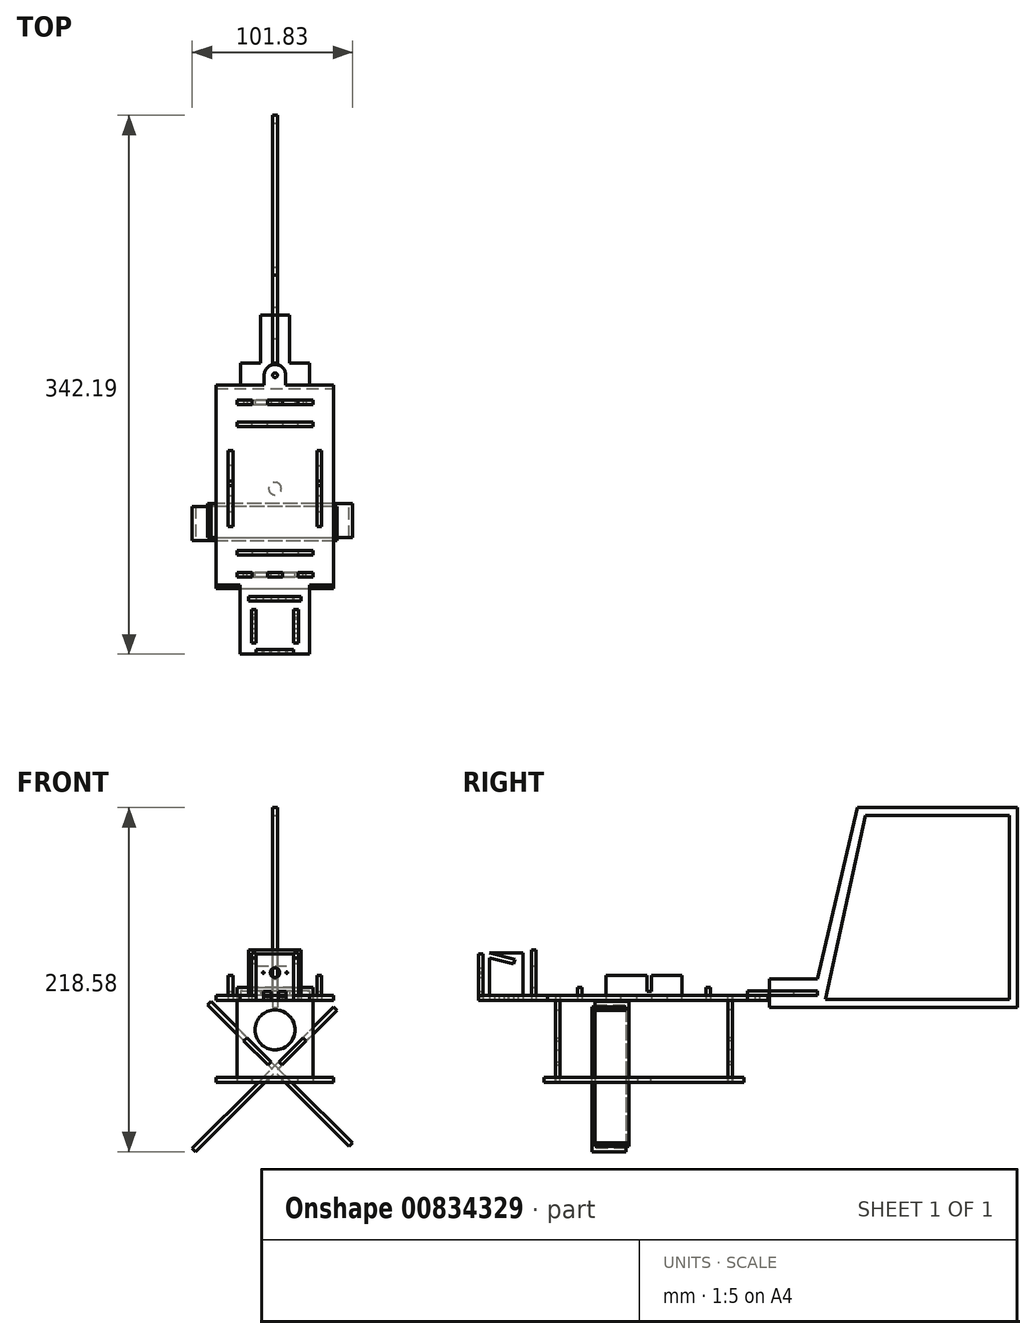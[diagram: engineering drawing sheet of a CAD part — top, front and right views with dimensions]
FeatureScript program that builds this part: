
annotation { "Feature Type Name" : "Feature", "Feature Type Description" : "" }
export const myFeature = defineFeature(function(context is Context, id is Id, definition is map)
    precondition{}
    {
        {
            var Q0;
            Q0=qCreatedBy(makeId("Top.planeOp"),FACE);
            var sketch = newSketch(context, id + "F0", { "sketchPlane" : qUnion([Q0])});
            skLineSegment(sketch, "E0", {"start": v(-22.56, -56.64) * mm, "end": v(-22.56, -53.64) * mm});
            skLineSegment(sketch, "E1", {"start": v(-22.56, -53.64) * mm, "end": v(-12.9, -53.64) * mm});
            skLineSegment(sketch, "E2", {"start": v(-12.9, -53.64) * mm, "end": v(-12.9, -56.64) * mm});
            skLineSegment(sketch, "E3", {"start": v(-3.25, -56.64) * mm, "end": v(-3.25, -53.64) * mm});
            skLineSegment(sketch, "E4", {"start": v(-3.25, -53.64) * mm, "end": v(6.4, -53.64) * mm});
            skLineSegment(sketch, "E5", {"start": v(6.4, -53.64) * mm, "end": v(6.4, -56.64) * mm});
            skLineSegment(sketch, "E6", {"start": v(16.05, -56.64) * mm, "end": v(16.05, -53.64) * mm});
            skLineSegment(sketch, "E7", {"start": v(16.05, -53.64) * mm, "end": v(25.7, -53.64) * mm});
            skLineSegment(sketch, "E8", {"start": v(25.7, -53.64) * mm, "end": v(25.7, -56.64) * mm});
            skLineSegment(sketch, "E9", {"start": v(-22.56, -56.64) * mm, "end": v(-12.9, -56.64) * mm});
            skLineSegment(sketch, "E10", {"start": v(-3.25, -56.64) * mm, "end": v(6.4, -56.64) * mm});
            skLineSegment(sketch, "E11", {"start": v(16.05, -56.64) * mm, "end": v(25.7, -56.64) * mm});
            skLineSegment(sketch, "E12", {"start": v(-22.56, 53.04) * mm, "end": v(-22.56, 56.04) * mm});
            skLineSegment(sketch, "E13", {"start": v(-22.56, 56.04) * mm, "end": v(-12.9, 56.04) * mm});
            skLineSegment(sketch, "E14", {"start": v(-12.9, 56.04) * mm, "end": v(-12.9, 53.04) * mm});
            skLineSegment(sketch, "E15", {"start": v(-3.25, 53.04) * mm, "end": v(-3.25, 56.04) * mm});
            skLineSegment(sketch, "E16", {"start": v(-3.25, 56.04) * mm, "end": v(6.4, 56.04) * mm});
            skLineSegment(sketch, "E17", {"start": v(6.4, 56.04) * mm, "end": v(6.4, 53.04) * mm});
            skLineSegment(sketch, "E18", {"start": v(16.05, 53.04) * mm, "end": v(16.05, 56.04) * mm});
            skLineSegment(sketch, "E19", {"start": v(16.05, 56.04) * mm, "end": v(25.7, 56.04) * mm});
            skLineSegment(sketch, "E20", {"start": v(25.7, 56.04) * mm, "end": v(25.7, 53.04) * mm});
            skLineSegment(sketch, "E21", {"start": v(-22.56, 53.04) * mm, "end": v(-12.9, 53.04) * mm});
            skLineSegment(sketch, "E22", {"start": v(-3.25, 53.04) * mm, "end": v(6.4, 53.04) * mm});
            skLineSegment(sketch, "E23", {"start": v(16.05, 53.04) * mm, "end": v(25.7, 53.04) * mm});
            skLineSegment(sketch, "E24", {"start": v(38.88, 63.2) * mm, "end": v(38.88, -63.8) * mm});
            skLineSegment(sketch, "E25", {"start": v(-35.74, 63.2) * mm, "end": v(-35.74, -63.8) * mm});
            skLineSegment(sketch, "E26", {"start": v(-35.74, -63.8) * mm, "end": v(38.88, -63.8) * mm});
            skLineSegment(sketch, "E27", {"start": v(-35.74, 63.2) * mm, "end": v(38.88, 63.2) * mm});
            skCircle(sketch, "E28", {"center": v(1.57, -0.3) * mm, "radius": 4 * mm});
            skSolve(sketch);
        }
        {
            var Q0;
            Q0=makeQuery(id+"F0.imprint","IMPRINT",FACE,{"disambiguationData":[TD([[makeQuery(id+"F0.imprint","IMPRINT",EDGE,{"derivedFrom":sQuery(id+"F0.wireOp",EDGE,"E0")}),1.0]])]});
            extrude(context, id + "F1", {"entities" : qUnion([Q0]), "depth" : 3 * mm, "offsetDistance" : 25.4 * mm});
        }
        {
            var Q0;
            Q0=makeQuery(id+"F1.opExtrude","SWEPT_FACE",FACE,{"disambiguationData":[OSD([sQuery(id+"F0.wireOp",EDGE,"E1")])]});
            var sketch = newSketch(context, id + "F2", { "sketchPlane" : qUnion([Q0])});
            skPoint(sketch, "E29.0", {"position": v(-22.56, 3) * mm});
            skPoint(sketch, "E30.0", {"position": v(-12.9, 3) * mm});
            skPoint(sketch, "E31.0", {"position": v(-12.9, 0) * mm});
            skPoint(sketch, "E32.0", {"position": v(-22.56, 0) * mm});
            skPoint(sketch, "E33.0", {"position": v(6.4, 3) * mm});
            skPoint(sketch, "E34.0", {"position": v(-3.25, 3) * mm});
            skPoint(sketch, "E35.0", {"position": v(-3.25, 0) * mm});
            skPoint(sketch, "E36.0", {"position": v(6.4, 0) * mm});
            skPoint(sketch, "E37.0", {"position": v(25.7, 3) * mm});
            skPoint(sketch, "E38.0", {"position": v(16.05, 3) * mm});
            skPoint(sketch, "E39.0", {"position": v(16.05, 0) * mm});
            skPoint(sketch, "E40.0", {"position": v(25.7, 0) * mm});
            skLineSegment(sketch, "E41", {"start": v(-3, 10.92) * mm, "end": v(-0.97, 12.95) * mm});
            skLineSegment(sketch, "E42", {"start": v(6.14, 10.92) * mm, "end": v(4.11, 12.95) * mm});
            skLineSegment(sketch, "E43", {"start": v(-0.97, 12.95) * mm, "end": v(-16.24, 28.22) * mm});
            skLineSegment(sketch, "E44", {"start": v(-3, 10.92) * mm, "end": v(-18.27, 26.19) * mm});
            skLineSegment(sketch, "E45", {"start": v(-18.27, 26.19) * mm, "end": v(-16.24, 28.22) * mm});
            skLineSegment(sketch, "E46", {"start": v(4.11, 12.95) * mm, "end": v(19.38, 28.22) * mm});
            skLineSegment(sketch, "E47", {"start": v(6.14, 10.92) * mm, "end": v(21.4, 26.19) * mm});
            skLineSegment(sketch, "E48", {"start": v(21.4, 26.19) * mm, "end": v(19.38, 28.22) * mm});
            skCircle(sketch, "E49", {"center": v(1.57, 33.27) * mm, "radius": 12.7 * mm});
            skLineSegment(sketch, "E50", {"start": v(25.7, 0) * mm, "end": v(16.05, 0) * mm});
            skLineSegment(sketch, "E51", {"start": v(16.05, 0) * mm, "end": v(16.05, 3) * mm});
            skLineSegment(sketch, "E52", {"start": v(16.05, 3) * mm, "end": v(6.4, 3) * mm});
            skLineSegment(sketch, "E53", {"start": v(6.4, 3) * mm, "end": v(6.4, 0) * mm});
            skLineSegment(sketch, "E54", {"start": v(6.4, 0) * mm, "end": v(-3.25, 0) * mm});
            skLineSegment(sketch, "E55", {"start": v(-3.25, 0) * mm, "end": v(-3.25, 3) * mm});
            skLineSegment(sketch, "E56", {"start": v(-3.25, 3) * mm, "end": v(-12.9, 3) * mm});
            skLineSegment(sketch, "E57", {"start": v(-12.9, 3) * mm, "end": v(-12.9, 0) * mm});
            skLineSegment(sketch, "E58", {"start": v(-12.9, 0) * mm, "end": v(-22.56, 0) * mm});
            skLineSegment(sketch, "E59", {"start": v(-22.56, 55.07) * mm, "end": v(-12.9, 55.07) * mm});
            skLineSegment(sketch, "E60", {"start": v(-12.9, 55.07) * mm, "end": v(-12.9, 52.07) * mm});
            skLineSegment(sketch, "E61", {"start": v(-12.9, 52.07) * mm, "end": v(-3.25, 52.07) * mm});
            skLineSegment(sketch, "E62", {"start": v(-3.25, 52.07) * mm, "end": v(-3.25, 55.07) * mm});
            skLineSegment(sketch, "E63", {"start": v(-3.25, 55.07) * mm, "end": v(6.4, 55.07) * mm});
            skLineSegment(sketch, "E64", {"start": v(6.4, 55.07) * mm, "end": v(6.4, 52.07) * mm});
            skLineSegment(sketch, "E65", {"start": v(6.4, 52.07) * mm, "end": v(16.05, 52.07) * mm});
            skLineSegment(sketch, "E66", {"start": v(16.05, 52.07) * mm, "end": v(16.05, 55.07) * mm});
            skLineSegment(sketch, "E67", {"start": v(16.05, 55.07) * mm, "end": v(25.7, 55.07) * mm});
            skLineSegment(sketch, "E68", {"start": v(-22.56, 55.07) * mm, "end": v(-22.56, 0) * mm});
            skLineSegment(sketch, "E69", {"start": v(25.7, 55.07) * mm, "end": v(25.7, 0) * mm});
            skSolve(sketch);
        }
        {
            var Q0;
            Q0=makeQuery(id+"F2.imprint","IMPRINT",FACE,{"disambiguationData":[TD([[makeQuery(id+"F2.imprint","IMPRINT",EDGE,{"derivedFrom":sQuery(id+"F2.wireOp",EDGE,"E41")}),-1.0]])]});
            extrude(context, id + "F3", {"entities" : qUnion([Q0]), "depth" : 3 * mm, "offsetDistance" : 25.4 * mm});
        }
        {
            var Q0;
            Q0=makeQuery(id+"F1.opExtrude","SWEPT_FACE",FACE,{"disambiguationData":[OSD([sQuery(id+"F0.wireOp",EDGE,"E23")])]});
            var sketch = newSketch(context, id + "F4", { "sketchPlane" : qUnion([Q0])});
            skLineSegment(sketch, "E70", {"start": v(-6.14, 10.92) * mm, "end": v(-4.11, 12.95) * mm});
            skLineSegment(sketch, "E71", {"start": v(3, 10.92) * mm, "end": v(0.97, 12.95) * mm});
            skLineSegment(sketch, "E72", {"start": v(-4.11, 12.95) * mm, "end": v(-19.38, 28.22) * mm});
            skLineSegment(sketch, "E73", {"start": v(-6.14, 10.92) * mm, "end": v(-21.4, 26.19) * mm});
            skLineSegment(sketch, "E74", {"start": v(-21.4, 26.19) * mm, "end": v(-19.38, 28.22) * mm});
            skLineSegment(sketch, "E75", {"start": v(0.97, 12.95) * mm, "end": v(16.24, 28.22) * mm});
            skLineSegment(sketch, "E76", {"start": v(3, 10.92) * mm, "end": v(18.27, 26.19) * mm});
            skLineSegment(sketch, "E77", {"start": v(18.27, 26.19) * mm, "end": v(16.24, 28.22) * mm});
            skCircle(sketch, "E78", {"center": v(-1.57, 33.27) * mm, "radius": 12.7 * mm});
            skLineSegment(sketch, "E79", {"start": v(22.56, 0) * mm, "end": v(12.9, 0) * mm});
            skLineSegment(sketch, "E80", {"start": v(12.9, 0) * mm, "end": v(12.9, 3) * mm});
            skLineSegment(sketch, "E81", {"start": v(12.9, 3) * mm, "end": v(3.26, 3) * mm});
            skLineSegment(sketch, "E82", {"start": v(3.26, 3) * mm, "end": v(3.26, 0) * mm});
            skLineSegment(sketch, "E83", {"start": v(3.26, 0) * mm, "end": v(-6.4, 0) * mm});
            skLineSegment(sketch, "E84", {"start": v(-6.4, 0) * mm, "end": v(-6.4, 3) * mm});
            skLineSegment(sketch, "E85", {"start": v(-6.4, 3) * mm, "end": v(-16.05, 3) * mm});
            skLineSegment(sketch, "E86", {"start": v(-16.05, 3) * mm, "end": v(-16.05, 0) * mm});
            skLineSegment(sketch, "E87", {"start": v(-16.05, 0) * mm, "end": v(-25.7, 0) * mm});
            skLineSegment(sketch, "E88", {"start": v(-25.7, 55.07) * mm, "end": v(-16.05, 55.07) * mm});
            skLineSegment(sketch, "E89", {"start": v(-16.05, 55.07) * mm, "end": v(-16.05, 52.07) * mm});
            skLineSegment(sketch, "E90", {"start": v(-16.05, 52.07) * mm, "end": v(-6.4, 52.07) * mm});
            skLineSegment(sketch, "E91", {"start": v(-6.4, 52.07) * mm, "end": v(-6.4, 55.07) * mm});
            skLineSegment(sketch, "E92", {"start": v(-6.4, 55.07) * mm, "end": v(3.26, 55.07) * mm});
            skLineSegment(sketch, "E93", {"start": v(3.26, 55.07) * mm, "end": v(3.26, 52.07) * mm});
            skLineSegment(sketch, "E94", {"start": v(3.26, 52.07) * mm, "end": v(12.9, 52.07) * mm});
            skLineSegment(sketch, "E95", {"start": v(12.9, 52.07) * mm, "end": v(12.9, 55.07) * mm});
            skLineSegment(sketch, "E96", {"start": v(12.9, 55.07) * mm, "end": v(22.56, 55.07) * mm});
            skLineSegment(sketch, "E97", {"start": v(-25.7, 55.07) * mm, "end": v(-25.7, 0) * mm});
            skLineSegment(sketch, "E98", {"start": v(22.56, 55.07) * mm, "end": v(22.56, 0) * mm});
            skPoint(sketch, "E99.0", {"position": v(-25.7, 3) * mm});
            skPoint(sketch, "E100.0", {"position": v(-16.05, 3) * mm});
            skPoint(sketch, "E101.0", {"position": v(-16.05, 0) * mm});
            skPoint(sketch, "E102.0", {"position": v(-25.7, 0) * mm});
            skPoint(sketch, "E103.0", {"position": v(-6.4, 3) * mm});
            skPoint(sketch, "E104.0", {"position": v(-6.4, 0) * mm});
            skPoint(sketch, "E105.0", {"position": v(3.25, 3) * mm});
            skPoint(sketch, "E106.0", {"position": v(3.25, 0) * mm});
            skPoint(sketch, "E107.0", {"position": v(22.56, 0) * mm});
            skPoint(sketch, "E108.0", {"position": v(22.56, 3) * mm});
            skPoint(sketch, "E109.0", {"position": v(12.9, 3) * mm});
            skPoint(sketch, "E110.0", {"position": v(12.9, 0) * mm});
            skSolve(sketch);
        }
        {
            var Q0;
            Q0=makeQuery(id+"F4.imprint","IMPRINT",FACE,{"disambiguationData":[TD([[makeQuery(id+"F4.imprint","IMPRINT",EDGE,{"derivedFrom":sQuery(id+"F4.wireOp",EDGE,"E70")}),-1.0]])]});
            extrude(context, id + "F5", {"entities" : qUnion([Q0]), "depth" : 3 * mm, "offsetDistance" : 25.4 * mm});
        }
        {
            var Q0;
            Q0=makeQuery(id+"F5.opExtrude","SWEPT_FACE",FACE,{"disambiguationData":[OSD([sQuery(id+"F4.wireOp",EDGE,"E76")])]});
            var sketch = newSketch(context, id + "F6", { "sketchPlane" : qUnion([Q0])});
            skLineSegment(sketch, "E111", {"start": v(-31.44, 63.75) * mm, "end": v(-9.85, 63.75) * mm});
            skLineSegment(sketch, "E112", {"start": v(-31.44, 63.75) * mm, "end": v(-31.44, -63.25) * mm});
            skLineSegment(sketch, "E113", {"start": v(-31.44, -63.25) * mm, "end": v(-9.85, -63.25) * mm});
            skLineSegment(sketch, "E114", {"start": v(-9.85, -63.25) * mm, "end": v(-9.85, 63.75) * mm});
            skPoint(sketch, "E115.0", {"position": v(9.46, 59.18) * mm});
            skPoint(sketch, "E116.0", {"position": v(9.46, 62.18) * mm});
            skPoint(sketch, "E117.0", {"position": v(-9.85, -53.64) * mm});
            skPoint(sketch, "E118.0", {"position": v(-9.85, -56.64) * mm});
            skPoint(sketch, "E119.0", {"position": v(-31.43, 56.04) * mm});
            skPoint(sketch, "E120.0", {"position": v(-31.43, 53.04) * mm});
            skPoint(sketch, "E121.0", {"position": v(-9.84, 53.04) * mm});
            skPoint(sketch, "E122.0", {"position": v(-9.84, 56.04) * mm});
            skSolve(sketch);
        }
        {
            var Q0;
            {var subQ5=sQuery(id+"F6.wireOp",EDGE,"E111");Q0=makeQuery(id+"F6.imprint","IMPRINT",FACE,{"disambiguationData":[TD([[makeQuery(id+"F6.imprint","IMPRINT",EDGE,{"derivedFrom":subQ5}),-1.0]])]});}
            extrude(context, id + "F7", {"entities" : qUnion([Q0]), "depth" : 3 * mm, "offsetDistance" : 25.4 * mm});
        }
        {
            var Q0;
            Q0=makeQuery(id+"F5.opExtrude","SWEPT_FACE",FACE,{"disambiguationData":[OSD([sQuery(id+"F4.wireOp",EDGE,"E73")])]});
            var sketch = newSketch(context, id + "F8", { "sketchPlane" : qUnion([Q0])});
            skLineSegment(sketch, "E123", {"start": v(11.73, 61.21) * mm, "end": v(33.32, 61.21) * mm});
            skLineSegment(sketch, "E124", {"start": v(11.73, 61.21) * mm, "end": v(11.73, -65.79) * mm});
            skLineSegment(sketch, "E125", {"start": v(11.73, -65.79) * mm, "end": v(33.32, -65.79) * mm});
            skLineSegment(sketch, "E126", {"start": v(33.32, -65.79) * mm, "end": v(33.32, 61.21) * mm});
            skPoint(sketch, "E127.0", {"position": v(33.66, 53.04) * mm});
            skPoint(sketch, "E128.0", {"position": v(33.66, 56.04) * mm});
            skPoint(sketch, "E129.0", {"position": v(12.07, 53.04) * mm});
            skPoint(sketch, "E130.0", {"position": v(12.07, 56.04) * mm});
            skPoint(sketch, "E131.0", {"position": v(12.07, -53.64) * mm});
            skPoint(sketch, "E132.0", {"position": v(12.07, -56.64) * mm});
            skPoint(sketch, "E133.0", {"position": v(33.66, -56.64) * mm});
            skPoint(sketch, "E134.0", {"position": v(33.66, -53.64) * mm});
            skSolve(sketch);
        }
        {
            var Q0;
            {var subQ5=sQuery(id+"F8.wireOp",EDGE,"E123");Q0=makeQuery(id+"F8.imprint","IMPRINT",FACE,{"disambiguationData":[TD([[makeQuery(id+"F8.imprint","IMPRINT",EDGE,{"derivedFrom":subQ5}),-1.0]])]});}
            extrude(context, id + "F9", {"entities" : qUnion([Q0]), "depth" : 3 * mm, "offsetDistance" : 25.4 * mm});
        }
        {
            var Q0;
            Q0=makeQuery(id+"F5.opExtrude","SWEPT_FACE",FACE,{"disambiguationData":[OSD([sQuery(id+"F4.wireOp",EDGE,"E90")])]});
            var sketch = newSketch(context, id + "F10", { "sketchPlane" : qUnion([Q0])});
            skLineSegment(sketch, "E135", {"start": v(8.72, -105.41) * mm, "end": v(3.95, -105.41) * mm});
            skLineSegment(sketch, "E136", {"start": v(3.95, -105.41) * mm, "end": v(3.95, -102.41) * mm});
            skLineSegment(sketch, "E137", {"start": v(3.95, -102.41) * mm, "end": v(-0.81, -102.41) * mm});
            skLineSegment(sketch, "E138", {"start": v(-0.81, -102.41) * mm, "end": v(-0.81, -105.41) * mm});
            skLineSegment(sketch, "E139", {"start": v(-0.81, -105.41) * mm, "end": v(-5.58, -105.41) * mm});
            skLineSegment(sketch, "E140", {"start": v(-5.58, -105.41) * mm, "end": v(-5.58, -102.41) * mm});
            skLineSegment(sketch, "E141", {"start": v(-5.58, -102.41) * mm, "end": v(-10.34, -102.41) * mm});
            skLineSegment(sketch, "E142", {"start": v(-10.34, -102.41) * mm, "end": v(-10.34, -105.41) * mm});
            skLineSegment(sketch, "E143", {"start": v(8.72, -105.41) * mm, "end": v(8.72, -102.41) * mm});
            skLineSegment(sketch, "E144", {"start": v(8.72, -102.41) * mm, "end": v(13.48, -102.41) * mm});
            skLineSegment(sketch, "E145", {"start": v(13.48, -102.41) * mm, "end": v(13.48, -105.41) * mm});
            skLineSegment(sketch, "E146", {"start": v(-10.34, -105.41) * mm, "end": v(-20.5, -105.41) * mm});
            skLineSegment(sketch, "E147", {"start": v(-20.5, -105.41) * mm, "end": v(-20.5, -61.67) * mm});
            skLineSegment(sketch, "E148", {"start": v(13.48, -105.41) * mm, "end": v(23.64, -105.41) * mm});
            skLineSegment(sketch, "E149", {"start": v(23.64, -105.41) * mm, "end": v(23.64, -61.67) * mm});
            skLineSegment(sketch, "E150", {"start": v(8.72, -71.83) * mm, "end": v(3.95, -71.83) * mm});
            skLineSegment(sketch, "E151", {"start": v(3.95, -71.83) * mm, "end": v(3.95, -68.83) * mm});
            skLineSegment(sketch, "E152", {"start": v(-0.81, -68.83) * mm, "end": v(-0.81, -71.83) * mm});
            skLineSegment(sketch, "E153", {"start": v(-0.81, -71.83) * mm, "end": v(-5.58, -71.83) * mm});
            skLineSegment(sketch, "E154", {"start": v(-5.58, -71.83) * mm, "end": v(-5.58, -68.83) * mm});
            skLineSegment(sketch, "E155", {"start": v(-10.34, -68.83) * mm, "end": v(-10.34, -71.83) * mm});
            skLineSegment(sketch, "E156", {"start": v(8.72, -71.83) * mm, "end": v(8.72, -68.83) * mm});
            skLineSegment(sketch, "E157", {"start": v(13.48, -68.83) * mm, "end": v(13.48, -71.83) * mm});
            skLineSegment(sketch, "E158", {"start": v(-10.34, -71.83) * mm, "end": v(-15.1, -71.83) * mm});
            skLineSegment(sketch, "E159", {"start": v(-15.1, -71.83) * mm, "end": v(-15.1, -68.83) * mm});
            skLineSegment(sketch, "E160", {"start": v(13.48, -71.83) * mm, "end": v(18.25, -71.83) * mm});
            skLineSegment(sketch, "E161", {"start": v(18.25, -71.83) * mm, "end": v(18.25, -68.83) * mm});
            skLineSegment(sketch, "E162", {"start": v(-15.1, -68.83) * mm, "end": v(-10.34, -68.83) * mm});
            skLineSegment(sketch, "E163", {"start": v(-5.58, -68.83) * mm, "end": v(-0.81, -68.83) * mm});
            skLineSegment(sketch, "E164", {"start": v(3.95, -68.83) * mm, "end": v(8.72, -68.83) * mm});
            skLineSegment(sketch, "E165", {"start": v(13.48, -68.83) * mm, "end": v(18.25, -68.83) * mm});
            skLineSegment(sketch, "E166", {"start": v(-10.34, -92.25) * mm, "end": v(-13.34, -92.25) * mm});
            skLineSegment(sketch, "E167", {"start": v(-13.34, -92.25) * mm, "end": v(-13.34, -89.23) * mm});
            skLineSegment(sketch, "E168", {"start": v(-13.34, -89.23) * mm, "end": v(-10.34, -89.23) * mm});
            skLineSegment(sketch, "E169", {"start": v(-10.34, -86.23) * mm, "end": v(-13.34, -86.23) * mm});
            skLineSegment(sketch, "E170", {"start": v(-13.34, -86.23) * mm, "end": v(-13.34, -83.23) * mm});
            skLineSegment(sketch, "E171", {"start": v(-13.34, -83.23) * mm, "end": v(-10.34, -83.23) * mm});
            skLineSegment(sketch, "E172", {"start": v(-10.34, -83.23) * mm, "end": v(-10.34, -86.23) * mm});
            skLineSegment(sketch, "E173", {"start": v(-10.34, -92.25) * mm, "end": v(-10.34, -89.23) * mm});
            skLineSegment(sketch, "E174", {"start": v(-20.5, -61.67) * mm, "end": v(-35.74, -61.67) * mm});
            skLineSegment(sketch, "E175", {"start": v(38.88, -61.67) * mm, "end": v(23.64, -61.67) * mm});
            skLineSegment(sketch, "E176", {"start": v(-22.56, -56.64) * mm, "end": v(-22.56, -53.64) * mm});
            skLineSegment(sketch, "E177", {"start": v(-22.56, -53.64) * mm, "end": v(-12.9, -53.64) * mm});
            skLineSegment(sketch, "E178", {"start": v(-12.9, -53.64) * mm, "end": v(-12.9, -56.64) * mm});
            skLineSegment(sketch, "E179", {"start": v(-3.25, -56.64) * mm, "end": v(-3.25, -53.64) * mm});
            skLineSegment(sketch, "E180", {"start": v(-3.25, -53.64) * mm, "end": v(6.4, -53.64) * mm});
            skLineSegment(sketch, "E181", {"start": v(6.4, -53.64) * mm, "end": v(6.4, -56.64) * mm});
            skLineSegment(sketch, "E182", {"start": v(16.05, -56.64) * mm, "end": v(16.05, -53.64) * mm});
            skLineSegment(sketch, "E183", {"start": v(16.05, -53.64) * mm, "end": v(25.7, -53.64) * mm});
            skLineSegment(sketch, "E184", {"start": v(25.7, -53.64) * mm, "end": v(25.7, -56.64) * mm});
            skLineSegment(sketch, "E185", {"start": v(-22.56, -56.64) * mm, "end": v(-12.9, -56.64) * mm});
            skLineSegment(sketch, "E186", {"start": v(-3.25, -56.64) * mm, "end": v(6.4, -56.64) * mm});
            skLineSegment(sketch, "E187", {"start": v(16.05, -56.64) * mm, "end": v(25.7, -56.64) * mm});
            skLineSegment(sketch, "E188", {"start": v(-22.56, 53.04) * mm, "end": v(-22.56, 56.04) * mm});
            skLineSegment(sketch, "E189", {"start": v(-22.56, 56.04) * mm, "end": v(-12.9, 56.04) * mm});
            skLineSegment(sketch, "E190", {"start": v(-12.9, 56.04) * mm, "end": v(-12.9, 53.04) * mm});
            skLineSegment(sketch, "E191", {"start": v(-3.25, 53.04) * mm, "end": v(-3.25, 56.04) * mm});
            skLineSegment(sketch, "E192", {"start": v(-3.25, 56.04) * mm, "end": v(6.4, 56.04) * mm});
            skLineSegment(sketch, "E193", {"start": v(6.4, 56.04) * mm, "end": v(6.4, 53.04) * mm});
            skLineSegment(sketch, "E194", {"start": v(16.05, 53.04) * mm, "end": v(16.05, 56.04) * mm});
            skLineSegment(sketch, "E195", {"start": v(16.05, 56.04) * mm, "end": v(25.7, 56.04) * mm});
            skLineSegment(sketch, "E196", {"start": v(25.7, 56.04) * mm, "end": v(25.7, 53.04) * mm});
            skLineSegment(sketch, "E197", {"start": v(-22.56, 53.04) * mm, "end": v(-12.9, 53.04) * mm});
            skLineSegment(sketch, "E198", {"start": v(-3.25, 53.04) * mm, "end": v(6.4, 53.04) * mm});
            skLineSegment(sketch, "E199", {"start": v(16.05, 53.04) * mm, "end": v(25.7, 53.04) * mm});
            skLineSegment(sketch, "E200", {"start": v(-35.74, -61.67) * mm, "end": v(-35.74, 65.33) * mm});
            skLineSegment(sketch, "E201", {"start": v(38.88, -61.67) * mm, "end": v(38.88, 65.33) * mm});
            skLineSegment(sketch, "E202", {"start": v(-35.74, 65.33) * mm, "end": v(-5.26, 65.33) * mm});
            skLineSegment(sketch, "E203", {"start": v(38.88, 65.33) * mm, "end": v(8.4, 65.33) * mm});
            skArc(sketch, "E204", {"start": v(8.4, 71.68) * mm, "mid": v(1.57, 78.5) * mm, "end": v(-5.26, 71.68) * mm});
            skCircle(sketch, "E205", {"center": v(1.57, 71.68) * mm, "radius": 1.5 * mm});
            skLineSegment(sketch, "E206", {"start": v(-5.26, 65.33) * mm, "end": v(-5.26, 71.68) * mm});
            skLineSegment(sketch, "E207", {"start": v(8.4, 65.33) * mm, "end": v(8.4, 71.68) * mm});
            skLineSegment(sketch, "E208", {"start": v(-22.56, 39.07) * mm, "end": v(-22.56, 42.07) * mm});
            skLineSegment(sketch, "E209", {"start": v(-22.56, 42.07) * mm, "end": v(-12.9, 42.07) * mm});
            skLineSegment(sketch, "E210", {"start": v(-12.9, 42.07) * mm, "end": v(-12.9, 39.07) * mm});
            skLineSegment(sketch, "E211", {"start": v(-3.25, 39.07) * mm, "end": v(-3.25, 42.07) * mm});
            skLineSegment(sketch, "E212", {"start": v(-3.25, 42.07) * mm, "end": v(6.4, 42.07) * mm});
            skLineSegment(sketch, "E213", {"start": v(6.4, 42.07) * mm, "end": v(6.4, 39.07) * mm});
            skLineSegment(sketch, "E214", {"start": v(16.05, 39.07) * mm, "end": v(16.05, 42.07) * mm});
            skLineSegment(sketch, "E215", {"start": v(16.05, 42.07) * mm, "end": v(25.7, 42.07) * mm});
            skLineSegment(sketch, "E216", {"start": v(25.7, 42.07) * mm, "end": v(25.7, 39.07) * mm});
            skLineSegment(sketch, "E217", {"start": v(-22.56, 39.07) * mm, "end": v(-12.9, 39.07) * mm});
            skLineSegment(sketch, "E218", {"start": v(-3.25, 39.07) * mm, "end": v(6.4, 39.07) * mm});
            skLineSegment(sketch, "E219", {"start": v(16.05, 39.07) * mm, "end": v(25.7, 39.07) * mm});
            skLineSegment(sketch, "E220", {"start": v(-22.56, -42.67) * mm, "end": v(-22.56, -39.67) * mm});
            skLineSegment(sketch, "E221", {"start": v(-22.56, -39.67) * mm, "end": v(-12.9, -39.67) * mm});
            skLineSegment(sketch, "E222", {"start": v(-12.9, -39.67) * mm, "end": v(-12.9, -42.67) * mm});
            skLineSegment(sketch, "E223", {"start": v(-3.25, -42.67) * mm, "end": v(-3.25, -39.67) * mm});
            skLineSegment(sketch, "E224", {"start": v(-3.25, -39.67) * mm, "end": v(6.4, -39.67) * mm});
            skLineSegment(sketch, "E225", {"start": v(6.4, -39.67) * mm, "end": v(6.4, -42.67) * mm});
            skLineSegment(sketch, "E226", {"start": v(16.05, -42.67) * mm, "end": v(16.05, -39.67) * mm});
            skLineSegment(sketch, "E227", {"start": v(16.05, -39.67) * mm, "end": v(25.7, -39.67) * mm});
            skLineSegment(sketch, "E228", {"start": v(25.7, -39.67) * mm, "end": v(25.7, -42.67) * mm});
            skLineSegment(sketch, "E229", {"start": v(-22.56, -42.67) * mm, "end": v(-12.9, -42.67) * mm});
            skLineSegment(sketch, "E230", {"start": v(-3.25, -42.67) * mm, "end": v(6.4, -42.67) * mm});
            skLineSegment(sketch, "E231", {"start": v(16.05, -42.67) * mm, "end": v(25.7, -42.67) * mm});
            skLineSegment(sketch, "E232", {"start": v(-28.1, 23.83) * mm, "end": v(-25.1, 23.83) * mm});
            skLineSegment(sketch, "E233", {"start": v(-25.1, 23.83) * mm, "end": v(-25.1, 14.17) * mm});
            skLineSegment(sketch, "E234", {"start": v(-25.1, 14.17) * mm, "end": v(-28.1, 14.17) * mm});
            skLineSegment(sketch, "E235", {"start": v(-28.1, 4.52) * mm, "end": v(-25.1, 4.52) * mm});
            skLineSegment(sketch, "E236", {"start": v(-25.1, 4.52) * mm, "end": v(-25.1, -5.13) * mm});
            skLineSegment(sketch, "E237", {"start": v(-25.1, -5.13) * mm, "end": v(-28.1, -5.13) * mm});
            skLineSegment(sketch, "E238", {"start": v(-28.1, -14.78) * mm, "end": v(-25.1, -14.78) * mm});
            skLineSegment(sketch, "E239", {"start": v(-25.1, -14.78) * mm, "end": v(-25.1, -24.43) * mm});
            skLineSegment(sketch, "E240", {"start": v(-25.1, -24.43) * mm, "end": v(-28.1, -24.43) * mm});
            skLineSegment(sketch, "E241", {"start": v(-28.1, 23.83) * mm, "end": v(-28.1, 14.17) * mm});
            skLineSegment(sketch, "E242", {"start": v(-28.1, 4.52) * mm, "end": v(-28.1, -5.13) * mm});
            skLineSegment(sketch, "E243", {"start": v(-28.1, -14.78) * mm, "end": v(-28.1, -24.43) * mm});
            skLineSegment(sketch, "E244", {"start": v(28.24, 23.83) * mm, "end": v(31.24, 23.83) * mm});
            skLineSegment(sketch, "E245", {"start": v(31.24, 23.83) * mm, "end": v(31.24, 14.17) * mm});
            skLineSegment(sketch, "E246", {"start": v(31.24, 14.17) * mm, "end": v(28.24, 14.17) * mm});
            skLineSegment(sketch, "E247", {"start": v(28.24, 4.52) * mm, "end": v(31.24, 4.52) * mm});
            skLineSegment(sketch, "E248", {"start": v(31.24, 4.52) * mm, "end": v(31.24, -5.13) * mm});
            skLineSegment(sketch, "E249", {"start": v(31.24, -5.13) * mm, "end": v(28.24, -5.13) * mm});
            skLineSegment(sketch, "E250", {"start": v(28.24, -14.78) * mm, "end": v(31.24, -14.78) * mm});
            skLineSegment(sketch, "E251", {"start": v(31.24, -14.78) * mm, "end": v(31.24, -24.43) * mm});
            skLineSegment(sketch, "E252", {"start": v(31.24, -24.43) * mm, "end": v(28.24, -24.43) * mm});
            skLineSegment(sketch, "E253", {"start": v(28.24, 23.83) * mm, "end": v(28.24, 14.17) * mm});
            skLineSegment(sketch, "E254", {"start": v(28.24, 4.52) * mm, "end": v(28.24, -5.13) * mm});
            skLineSegment(sketch, "E255", {"start": v(28.24, -14.78) * mm, "end": v(28.24, -24.43) * mm});
            skLineSegment(sketch, "E256", {"start": v(-10.34, -80.23) * mm, "end": v(-13.34, -80.23) * mm});
            skLineSegment(sketch, "E257", {"start": v(-13.34, -80.23) * mm, "end": v(-13.34, -77.23) * mm});
            skLineSegment(sketch, "E258", {"start": v(-13.34, -77.23) * mm, "end": v(-10.34, -77.23) * mm});
            skLineSegment(sketch, "E259", {"start": v(-10.34, -77.23) * mm, "end": v(-10.34, -80.23) * mm});
            skLineSegment(sketch, "E260", {"start": v(-10.34, -98.25) * mm, "end": v(-13.34, -98.25) * mm});
            skLineSegment(sketch, "E261", {"start": v(-13.34, -98.25) * mm, "end": v(-13.34, -95.25) * mm});
            skLineSegment(sketch, "E262", {"start": v(-13.34, -95.25) * mm, "end": v(-10.34, -95.25) * mm});
            skLineSegment(sketch, "E263", {"start": v(-10.34, -95.25) * mm, "end": v(-10.34, -98.25) * mm});
            skLineSegment(sketch, "E264", {"start": v(16.48, -92.25) * mm, "end": v(13.48, -92.25) * mm});
            skLineSegment(sketch, "E265", {"start": v(13.48, -92.25) * mm, "end": v(13.48, -89.23) * mm});
            skLineSegment(sketch, "E266", {"start": v(13.48, -89.23) * mm, "end": v(16.48, -89.23) * mm});
            skLineSegment(sketch, "E267", {"start": v(16.48, -86.23) * mm, "end": v(13.48, -86.23) * mm});
            skLineSegment(sketch, "E268", {"start": v(13.48, -86.23) * mm, "end": v(13.48, -83.23) * mm});
            skLineSegment(sketch, "E269", {"start": v(13.48, -83.23) * mm, "end": v(16.48, -83.23) * mm});
            skLineSegment(sketch, "E270", {"start": v(16.48, -83.23) * mm, "end": v(16.48, -86.23) * mm});
            skLineSegment(sketch, "E271", {"start": v(16.48, -92.25) * mm, "end": v(16.48, -89.23) * mm});
            skLineSegment(sketch, "E272", {"start": v(16.48, -80.23) * mm, "end": v(13.48, -80.23) * mm});
            skLineSegment(sketch, "E273", {"start": v(13.48, -80.23) * mm, "end": v(13.48, -77.23) * mm});
            skLineSegment(sketch, "E274", {"start": v(13.48, -77.23) * mm, "end": v(16.48, -77.23) * mm});
            skLineSegment(sketch, "E275", {"start": v(16.48, -77.23) * mm, "end": v(16.48, -80.23) * mm});
            skLineSegment(sketch, "E276", {"start": v(16.48, -98.25) * mm, "end": v(13.48, -98.25) * mm});
            skLineSegment(sketch, "E277", {"start": v(13.48, -98.25) * mm, "end": v(13.48, -95.25) * mm});
            skLineSegment(sketch, "E278", {"start": v(13.48, -95.25) * mm, "end": v(16.48, -95.25) * mm});
            skLineSegment(sketch, "E279", {"start": v(16.48, -95.25) * mm, "end": v(16.48, -98.25) * mm});
            skPoint(sketch, "E280.0", {"position": v(-12.9, 56.04) * mm});
            skPoint(sketch, "E281.0", {"position": v(-12.9, 53.04) * mm});
            skPoint(sketch, "E282.0", {"position": v(-3.25, 53.04) * mm});
            skPoint(sketch, "E283.0", {"position": v(-3.25, 56.04) * mm});
            skPoint(sketch, "E284.0", {"position": v(-22.56, 53.04) * mm});
            skPoint(sketch, "E285.0", {"position": v(-22.56, 56.04) * mm});
            skPoint(sketch, "E286.0", {"position": v(25.7, 56.04) * mm});
            skPoint(sketch, "E287.0", {"position": v(25.7, 53.04) * mm});
            skPoint(sketch, "E288.0", {"position": v(-22.56, -53.64) * mm});
            skPoint(sketch, "E289.0", {"position": v(-22.56, -56.64) * mm});
            skPoint(sketch, "E290.0", {"position": v(-12.9, -56.64) * mm});
            skPoint(sketch, "E291.0", {"position": v(-12.9, -53.64) * mm});
            skPoint(sketch, "E292.0", {"position": v(-3.25, -53.64) * mm});
            skPoint(sketch, "E293.0", {"position": v(-3.25, -56.64) * mm});
            skPoint(sketch, "E294.0", {"position": v(6.4, -56.64) * mm});
            skPoint(sketch, "E295.0", {"position": v(6.4, -53.64) * mm});
            skPoint(sketch, "E296.0", {"position": v(16.05, -53.64) * mm});
            skPoint(sketch, "E297.0", {"position": v(16.05, -56.64) * mm});
            skPoint(sketch, "E298.0", {"position": v(25.7, -56.64) * mm});
            skPoint(sketch, "E299.0", {"position": v(25.7, -53.64) * mm});
            skPoint(sketch, "E300.0", {"position": v(6.4, 56.04) * mm});
            skPoint(sketch, "E301.0", {"position": v(6.4, 53.04) * mm});
            skPoint(sketch, "E302.0", {"position": v(16.05, 53.04) * mm});
            skPoint(sketch, "E303.0", {"position": v(16.05, 56.04) * mm});
            skPoint(sketch, "E304.0", {"position": v(-22.8, -56.88) * mm});
            skPoint(sketch, "E305.0", {"position": v(-22.8, -53.88) * mm});
            skPoint(sketch, "E306.0", {"position": v(-13.14, -56.88) * mm});
            skPoint(sketch, "E307.0", {"position": v(-13.14, -53.88) * mm});
            skPoint(sketch, "E308.0", {"position": v(-3.49, -56.88) * mm});
            skPoint(sketch, "E309.0", {"position": v(6.16, -56.88) * mm});
            skPoint(sketch, "E310.0", {"position": v(6.16, -53.88) * mm});
            skPoint(sketch, "E311.0", {"position": v(-3.49, -53.88) * mm});
            skPoint(sketch, "E312.0", {"position": v(-22.8, 55.8) * mm});
            skPoint(sketch, "E313.0", {"position": v(-22.8, 52.8) * mm});
            skPoint(sketch, "E314.0", {"position": v(-13.14, 52.8) * mm});
            skPoint(sketch, "E315.0", {"position": v(-13.14, 55.8) * mm});
            skPoint(sketch, "E316.0", {"position": v(-3.49, 52.8) * mm});
            skPoint(sketch, "E317.0", {"position": v(6.16, 52.8) * mm});
            skPoint(sketch, "E318.0", {"position": v(6.16, 55.8) * mm});
            skPoint(sketch, "E319.0", {"position": v(-3.49, 55.8) * mm});
            skSolve(sketch);
        }
        {
            var Q0;
            Q0=makeQuery(id+"F10.imprint","IMPRINT",FACE,{"disambiguationData":[TD([[makeQuery(id+"F10.imprint","IMPRINT",EDGE,{"derivedFrom":sQuery(id+"F10.wireOp",EDGE,"E135")}),-1.0]])]});
            extrude(context, id + "F11", {"entities" : qUnion([Q0]), "depth" : 3 * mm, "offsetDistance" : 25.4 * mm});
        }
        {
            var Q0;
            Q0=makeQuery(id+"F11.opExtrude","CAP_FACE",FACE,{"disambiguationData":[OSD([sQuery(id+"F4.wireOp",EDGE,"E90"),sQuery(id+"F10.wireOp",EDGE,"E135"),sQuery(id+"F10.wireOp",EDGE,"E136"),sQuery(id+"F10.wireOp",EDGE,"E137"),sQuery(id+"F10.wireOp",EDGE,"E138"),sQuery(id+"F10.wireOp",EDGE,"E139"),sQuery(id+"F10.wireOp",EDGE,"E140"),sQuery(id+"F10.wireOp",EDGE,"E141"),sQuery(id+"F10.wireOp",EDGE,"E142"),sQuery(id+"F10.wireOp",EDGE,"E143"),sQuery(id+"F10.wireOp",EDGE,"E144"),sQuery(id+"F10.wireOp",EDGE,"E145"),sQuery(id+"F10.wireOp",EDGE,"E146"),sQuery(id+"F10.wireOp",EDGE,"E147"),sQuery(id+"F10.wireOp",EDGE,"E148"),sQuery(id+"F10.wireOp",EDGE,"E149"),sQuery(id+"F10.wireOp",EDGE,"E150"),sQuery(id+"F10.wireOp",EDGE,"E151"),sQuery(id+"F10.wireOp",EDGE,"E152"),sQuery(id+"F10.wireOp",EDGE,"E153"),sQuery(id+"F10.wireOp",EDGE,"E154"),sQuery(id+"F10.wireOp",EDGE,"E155"),sQuery(id+"F10.wireOp",EDGE,"E156"),sQuery(id+"F10.wireOp",EDGE,"E157"),sQuery(id+"F10.wireOp",EDGE,"E158"),sQuery(id+"F10.wireOp",EDGE,"E159"),sQuery(id+"F10.wireOp",EDGE,"E160"),sQuery(id+"F10.wireOp",EDGE,"E161"),sQuery(id+"F10.wireOp",EDGE,"E162"),sQuery(id+"F10.wireOp",EDGE,"E163"),sQuery(id+"F10.wireOp",EDGE,"E164"),sQuery(id+"F10.wireOp",EDGE,"E165"),sQuery(id+"F10.wireOp",EDGE,"E166"),sQuery(id+"F10.wireOp",EDGE,"E167"),sQuery(id+"F10.wireOp",EDGE,"E168"),sQuery(id+"F10.wireOp",EDGE,"E169"),sQuery(id+"F10.wireOp",EDGE,"E170"),sQuery(id+"F10.wireOp",EDGE,"E171"),sQuery(id+"F10.wireOp",EDGE,"E172"),sQuery(id+"F10.wireOp",EDGE,"E173"),sQuery(id+"F10.wireOp",EDGE,"E174"),sQuery(id+"F10.wireOp",EDGE,"E175"),sQuery(id+"F10.wireOp",EDGE,"E176"),sQuery(id+"F10.wireOp",EDGE,"E177"),sQuery(id+"F10.wireOp",EDGE,"E178"),sQuery(id+"F10.wireOp",EDGE,"E179"),sQuery(id+"F10.wireOp",EDGE,"E180"),sQuery(id+"F10.wireOp",EDGE,"E181"),sQuery(id+"F10.wireOp",EDGE,"E182"),sQuery(id+"F10.wireOp",EDGE,"E183"),sQuery(id+"F10.wireOp",EDGE,"E184"),sQuery(id+"F10.wireOp",EDGE,"E185"),sQuery(id+"F10.wireOp",EDGE,"E186"),sQuery(id+"F10.wireOp",EDGE,"E187"),sQuery(id+"F10.wireOp",EDGE,"E188"),sQuery(id+"F10.wireOp",EDGE,"E189"),sQuery(id+"F10.wireOp",EDGE,"E190"),sQuery(id+"F10.wireOp",EDGE,"E191"),sQuery(id+"F10.wireOp",EDGE,"E192"),sQuery(id+"F10.wireOp",EDGE,"E195"),sQuery(id+"F10.wireOp",EDGE,"E196"),sQuery(id+"F10.wireOp",EDGE,"E197"),sQuery(id+"F10.wireOp",EDGE,"E198"),sQuery(id+"F10.wireOp",EDGE,"E199"),sQuery(id+"F10.wireOp",EDGE,"E200"),sQuery(id+"F10.wireOp",EDGE,"E201"),sQuery(id+"F10.wireOp",EDGE,"E202"),sQuery(id+"F10.wireOp",EDGE,"E203"),sQuery(id+"F10.wireOp",EDGE,"E204"),sQuery(id+"F10.wireOp",EDGE,"E205"),sQuery(id+"F10.wireOp",EDGE,"E206"),sQuery(id+"F10.wireOp",EDGE,"E207"),sQuery(id+"F10.wireOp",EDGE,"E208"),sQuery(id+"F10.wireOp",EDGE,"E209"),sQuery(id+"F10.wireOp",EDGE,"E210"),sQuery(id+"F10.wireOp",EDGE,"E211"),sQuery(id+"F10.wireOp",EDGE,"E212"),sQuery(id+"F10.wireOp",EDGE,"E213"),sQuery(id+"F10.wireOp",EDGE,"E214"),sQuery(id+"F10.wireOp",EDGE,"E215"),sQuery(id+"F10.wireOp",EDGE,"E216"),sQuery(id+"F10.wireOp",EDGE,"E217"),sQuery(id+"F10.wireOp",EDGE,"E218"),sQuery(id+"F10.wireOp",EDGE,"E219"),sQuery(id+"F10.wireOp",EDGE,"E220"),sQuery(id+"F10.wireOp",EDGE,"E221"),sQuery(id+"F10.wireOp",EDGE,"E222"),sQuery(id+"F10.wireOp",EDGE,"E223"),sQuery(id+"F10.wireOp",EDGE,"E224"),sQuery(id+"F10.wireOp",EDGE,"E225"),sQuery(id+"F10.wireOp",EDGE,"E226"),sQuery(id+"F10.wireOp",EDGE,"E227"),sQuery(id+"F10.wireOp",EDGE,"E228"),sQuery(id+"F10.wireOp",EDGE,"E229"),sQuery(id+"F10.wireOp",EDGE,"E230"),sQuery(id+"F10.wireOp",EDGE,"E231"),sQuery(id+"F10.wireOp",EDGE,"E232"),sQuery(id+"F10.wireOp",EDGE,"E233"),sQuery(id+"F10.wireOp",EDGE,"E234"),sQuery(id+"F10.wireOp",EDGE,"E235"),sQuery(id+"F10.wireOp",EDGE,"E236"),sQuery(id+"F10.wireOp",EDGE,"E237"),sQuery(id+"F10.wireOp",EDGE,"E238"),sQuery(id+"F10.wireOp",EDGE,"E239"),sQuery(id+"F10.wireOp",EDGE,"E240"),sQuery(id+"F10.wireOp",EDGE,"E241"),sQuery(id+"F10.wireOp",EDGE,"E242"),sQuery(id+"F10.wireOp",EDGE,"E243"),sQuery(id+"F10.wireOp",EDGE,"E244"),sQuery(id+"F10.wireOp",EDGE,"E245"),sQuery(id+"F10.wireOp",EDGE,"E246"),sQuery(id+"F10.wireOp",EDGE,"E247"),sQuery(id+"F10.wireOp",EDGE,"E248"),sQuery(id+"F10.wireOp",EDGE,"E249"),sQuery(id+"F10.wireOp",EDGE,"E250"),sQuery(id+"F10.wireOp",EDGE,"E251"),sQuery(id+"F10.wireOp",EDGE,"E252"),sQuery(id+"F10.wireOp",EDGE,"E253"),sQuery(id+"F10.wireOp",EDGE,"E254"),sQuery(id+"F10.wireOp",EDGE,"E255"),sQuery(id+"F10.wireOp",EDGE,"E256"),sQuery(id+"F10.wireOp",EDGE,"E257"),sQuery(id+"F10.wireOp",EDGE,"E258"),sQuery(id+"F10.wireOp",EDGE,"E259"),sQuery(id+"F10.wireOp",EDGE,"E260"),sQuery(id+"F10.wireOp",EDGE,"E261"),sQuery(id+"F10.wireOp",EDGE,"E262"),sQuery(id+"F10.wireOp",EDGE,"E263"),sQuery(id+"F10.wireOp",EDGE,"E264"),sQuery(id+"F10.wireOp",EDGE,"E265"),sQuery(id+"F10.wireOp",EDGE,"E266"),sQuery(id+"F10.wireOp",EDGE,"E267"),sQuery(id+"F10.wireOp",EDGE,"E268"),sQuery(id+"F10.wireOp",EDGE,"E269"),sQuery(id+"F10.wireOp",EDGE,"E270"),sQuery(id+"F10.wireOp",EDGE,"E271"),sQuery(id+"F10.wireOp",EDGE,"E272"),sQuery(id+"F10.wireOp",EDGE,"E273"),sQuery(id+"F10.wireOp",EDGE,"E274"),sQuery(id+"F10.wireOp",EDGE,"E275"),sQuery(id+"F10.wireOp",EDGE,"E276"),sQuery(id+"F10.wireOp",EDGE,"E277"),sQuery(id+"F10.wireOp",EDGE,"E278"),sQuery(id+"F10.wireOp",EDGE,"E279")])],"isStart":false});
            var Q1;
            Q1=makeQuery(id+"F11.opExtrude","CAP_FACE",FACE,{"disambiguationData":[OSD([sQuery(id+"F4.wireOp",EDGE,"E90"),sQuery(id+"F10.wireOp",EDGE,"E135"),sQuery(id+"F10.wireOp",EDGE,"E136"),sQuery(id+"F10.wireOp",EDGE,"E137"),sQuery(id+"F10.wireOp",EDGE,"E138"),sQuery(id+"F10.wireOp",EDGE,"E139"),sQuery(id+"F10.wireOp",EDGE,"E140"),sQuery(id+"F10.wireOp",EDGE,"E141"),sQuery(id+"F10.wireOp",EDGE,"E142"),sQuery(id+"F10.wireOp",EDGE,"E143"),sQuery(id+"F10.wireOp",EDGE,"E144"),sQuery(id+"F10.wireOp",EDGE,"E145"),sQuery(id+"F10.wireOp",EDGE,"E146"),sQuery(id+"F10.wireOp",EDGE,"E147"),sQuery(id+"F10.wireOp",EDGE,"E148"),sQuery(id+"F10.wireOp",EDGE,"E149"),sQuery(id+"F10.wireOp",EDGE,"E150"),sQuery(id+"F10.wireOp",EDGE,"E151"),sQuery(id+"F10.wireOp",EDGE,"E152"),sQuery(id+"F10.wireOp",EDGE,"E153"),sQuery(id+"F10.wireOp",EDGE,"E154"),sQuery(id+"F10.wireOp",EDGE,"E155"),sQuery(id+"F10.wireOp",EDGE,"E156"),sQuery(id+"F10.wireOp",EDGE,"E157"),sQuery(id+"F10.wireOp",EDGE,"E158"),sQuery(id+"F10.wireOp",EDGE,"E159"),sQuery(id+"F10.wireOp",EDGE,"E160"),sQuery(id+"F10.wireOp",EDGE,"E161"),sQuery(id+"F10.wireOp",EDGE,"E162"),sQuery(id+"F10.wireOp",EDGE,"E163"),sQuery(id+"F10.wireOp",EDGE,"E164"),sQuery(id+"F10.wireOp",EDGE,"E165"),sQuery(id+"F10.wireOp",EDGE,"E166"),sQuery(id+"F10.wireOp",EDGE,"E167"),sQuery(id+"F10.wireOp",EDGE,"E168"),sQuery(id+"F10.wireOp",EDGE,"E169"),sQuery(id+"F10.wireOp",EDGE,"E170"),sQuery(id+"F10.wireOp",EDGE,"E171"),sQuery(id+"F10.wireOp",EDGE,"E172"),sQuery(id+"F10.wireOp",EDGE,"E173"),sQuery(id+"F10.wireOp",EDGE,"E174"),sQuery(id+"F10.wireOp",EDGE,"E175"),sQuery(id+"F10.wireOp",EDGE,"E176"),sQuery(id+"F10.wireOp",EDGE,"E177"),sQuery(id+"F10.wireOp",EDGE,"E178"),sQuery(id+"F10.wireOp",EDGE,"E179"),sQuery(id+"F10.wireOp",EDGE,"E180"),sQuery(id+"F10.wireOp",EDGE,"E181"),sQuery(id+"F10.wireOp",EDGE,"E182"),sQuery(id+"F10.wireOp",EDGE,"E183"),sQuery(id+"F10.wireOp",EDGE,"E184"),sQuery(id+"F10.wireOp",EDGE,"E185"),sQuery(id+"F10.wireOp",EDGE,"E186"),sQuery(id+"F10.wireOp",EDGE,"E187"),sQuery(id+"F10.wireOp",EDGE,"E188"),sQuery(id+"F10.wireOp",EDGE,"E189"),sQuery(id+"F10.wireOp",EDGE,"E190"),sQuery(id+"F10.wireOp",EDGE,"E191"),sQuery(id+"F10.wireOp",EDGE,"E192"),sQuery(id+"F10.wireOp",EDGE,"E195"),sQuery(id+"F10.wireOp",EDGE,"E196"),sQuery(id+"F10.wireOp",EDGE,"E197"),sQuery(id+"F10.wireOp",EDGE,"E198"),sQuery(id+"F10.wireOp",EDGE,"E199"),sQuery(id+"F10.wireOp",EDGE,"E200"),sQuery(id+"F10.wireOp",EDGE,"E201"),sQuery(id+"F10.wireOp",EDGE,"E202"),sQuery(id+"F10.wireOp",EDGE,"E203"),sQuery(id+"F10.wireOp",EDGE,"E204"),sQuery(id+"F10.wireOp",EDGE,"E205"),sQuery(id+"F10.wireOp",EDGE,"E206"),sQuery(id+"F10.wireOp",EDGE,"E207"),sQuery(id+"F10.wireOp",EDGE,"E208"),sQuery(id+"F10.wireOp",EDGE,"E209"),sQuery(id+"F10.wireOp",EDGE,"E210"),sQuery(id+"F10.wireOp",EDGE,"E211"),sQuery(id+"F10.wireOp",EDGE,"E212"),sQuery(id+"F10.wireOp",EDGE,"E213"),sQuery(id+"F10.wireOp",EDGE,"E214"),sQuery(id+"F10.wireOp",EDGE,"E215"),sQuery(id+"F10.wireOp",EDGE,"E216"),sQuery(id+"F10.wireOp",EDGE,"E217"),sQuery(id+"F10.wireOp",EDGE,"E218"),sQuery(id+"F10.wireOp",EDGE,"E219"),sQuery(id+"F10.wireOp",EDGE,"E220"),sQuery(id+"F10.wireOp",EDGE,"E221"),sQuery(id+"F10.wireOp",EDGE,"E222"),sQuery(id+"F10.wireOp",EDGE,"E223"),sQuery(id+"F10.wireOp",EDGE,"E224"),sQuery(id+"F10.wireOp",EDGE,"E225"),sQuery(id+"F10.wireOp",EDGE,"E226"),sQuery(id+"F10.wireOp",EDGE,"E227"),sQuery(id+"F10.wireOp",EDGE,"E228"),sQuery(id+"F10.wireOp",EDGE,"E229"),sQuery(id+"F10.wireOp",EDGE,"E230"),sQuery(id+"F10.wireOp",EDGE,"E231"),sQuery(id+"F10.wireOp",EDGE,"E232"),sQuery(id+"F10.wireOp",EDGE,"E233"),sQuery(id+"F10.wireOp",EDGE,"E234"),sQuery(id+"F10.wireOp",EDGE,"E235"),sQuery(id+"F10.wireOp",EDGE,"E236"),sQuery(id+"F10.wireOp",EDGE,"E237"),sQuery(id+"F10.wireOp",EDGE,"E238"),sQuery(id+"F10.wireOp",EDGE,"E239"),sQuery(id+"F10.wireOp",EDGE,"E240"),sQuery(id+"F10.wireOp",EDGE,"E241"),sQuery(id+"F10.wireOp",EDGE,"E242"),sQuery(id+"F10.wireOp",EDGE,"E243"),sQuery(id+"F10.wireOp",EDGE,"E244"),sQuery(id+"F10.wireOp",EDGE,"E245"),sQuery(id+"F10.wireOp",EDGE,"E246"),sQuery(id+"F10.wireOp",EDGE,"E247"),sQuery(id+"F10.wireOp",EDGE,"E248"),sQuery(id+"F10.wireOp",EDGE,"E249"),sQuery(id+"F10.wireOp",EDGE,"E250"),sQuery(id+"F10.wireOp",EDGE,"E251"),sQuery(id+"F10.wireOp",EDGE,"E252"),sQuery(id+"F10.wireOp",EDGE,"E253"),sQuery(id+"F10.wireOp",EDGE,"E254"),sQuery(id+"F10.wireOp",EDGE,"E255"),sQuery(id+"F10.wireOp",EDGE,"E256"),sQuery(id+"F10.wireOp",EDGE,"E257"),sQuery(id+"F10.wireOp",EDGE,"E258"),sQuery(id+"F10.wireOp",EDGE,"E259"),sQuery(id+"F10.wireOp",EDGE,"E260"),sQuery(id+"F10.wireOp",EDGE,"E261"),sQuery(id+"F10.wireOp",EDGE,"E262"),sQuery(id+"F10.wireOp",EDGE,"E263"),sQuery(id+"F10.wireOp",EDGE,"E264"),sQuery(id+"F10.wireOp",EDGE,"E265"),sQuery(id+"F10.wireOp",EDGE,"E266"),sQuery(id+"F10.wireOp",EDGE,"E267"),sQuery(id+"F10.wireOp",EDGE,"E268"),sQuery(id+"F10.wireOp",EDGE,"E269"),sQuery(id+"F10.wireOp",EDGE,"E270"),sQuery(id+"F10.wireOp",EDGE,"E271"),sQuery(id+"F10.wireOp",EDGE,"E272"),sQuery(id+"F10.wireOp",EDGE,"E273"),sQuery(id+"F10.wireOp",EDGE,"E274"),sQuery(id+"F10.wireOp",EDGE,"E275"),sQuery(id+"F10.wireOp",EDGE,"E276"),sQuery(id+"F10.wireOp",EDGE,"E277"),sQuery(id+"F10.wireOp",EDGE,"E278"),sQuery(id+"F10.wireOp",EDGE,"E279")])],"isStart":false});
            var sketch = newSketch(context, id + "F12", { "sketchPlane" : qUnion([Q0, Q1])});
            skLineSegment(sketch, "E320", {"start": v(3.07, 94.54) * mm, "end": v(0.07, 94.54) * mm});
            skLineSegment(sketch, "E321", {"start": v(0.07, 94.54) * mm, "end": v(0.07, 109.78) * mm});
            skLineSegment(sketch, "E322", {"start": v(3.07, 94.54) * mm, "end": v(3.07, 109.78) * mm});
            skLineSegment(sketch, "E323", {"start": v(3.07, 109.78) * mm, "end": v(10.7, 109.78) * mm});
            skLineSegment(sketch, "E324", {"start": v(10.7, 109.78) * mm, "end": v(10.7, 79.3) * mm});
            skLineSegment(sketch, "E325", {"start": v(0.07, 109.78) * mm, "end": v(-7.55, 109.78) * mm});
            skLineSegment(sketch, "E326", {"start": v(-7.55, 109.78) * mm, "end": v(-7.55, 79.3) * mm});
            skLineSegment(sketch, "E327", {"start": v(-7.55, 79.3) * mm, "end": v(-20.25, 79.3) * mm});
            skLineSegment(sketch, "E328", {"start": v(10.7, 79.3) * mm, "end": v(23.4, 79.3) * mm});
            skLineSegment(sketch, "E329", {"start": v(-20.25, 79.3) * mm, "end": v(-20.25, 64.06) * mm});
            skLineSegment(sketch, "E330", {"start": v(23.4, 79.3) * mm, "end": v(23.4, 64.06) * mm});
            skLineSegment(sketch, "E331", {"start": v(23.4, 64.06) * mm, "end": v(-20.25, 64.06) * mm});
            skCircle(sketch, "E332", {"center": v(1.57, 71.68) * mm, "radius": 1.5 * mm});
            skSolve(sketch);
        }
        {
            var Q0;
            Q0=makeQuery(id+"F12.imprint","IMPRINT",FACE,{"disambiguationData":[TD([[makeQuery(id+"F12.imprint","IMPRINT",EDGE,{"derivedFrom":sQuery(id+"F12.wireOp",EDGE,"E320")}),1.0]])]});
            extrude(context, id + "F13", {"entities" : qUnion([Q0]), "depth" : 3 * mm, "offsetDistance" : 25.4 * mm});
        }
        {
            var Q0;
            Q0=makeQuery(id+"F13.opExtrude","SWEPT_FACE",FACE,{"disambiguationData":[OSD([sQuery(id+"F12.wireOp",EDGE,"E322")])]});
            var sketch = newSketch(context, id + "F14", { "sketchPlane" : qUnion([Q0])});
            skLineSegment(sketch, "E333", {"start": v(-236.78, 174.45) * mm, "end": v(-236.78, 47.45) * mm});
            skLineSegment(sketch, "E334", {"start": v(-236.78, 47.45) * mm, "end": v(-79.3, 47.45) * mm});
            skLineSegment(sketch, "E335", {"start": v(-236.78, 174.45) * mm, "end": v(-135.18, 174.45) * mm});
            skLineSegment(sketch, "E336", {"start": v(-231.7, 169.3) * mm, "end": v(-231.65, 52.53) * mm});
            skLineSegment(sketch, "E337", {"start": v(-114.86, 52.53) * mm, "end": v(-140.26, 169.37) * mm});
            skLineSegment(sketch, "E338", {"start": v(-140.26, 169.37) * mm, "end": v(-231.7, 169.3) * mm});
            skLineSegment(sketch, "E339", {"start": v(-231.65, 52.53) * mm, "end": v(-114.86, 52.53) * mm});
            skLineSegment(sketch, "E340", {"start": v(-94.54, 55.07) * mm, "end": v(-94.54, 58.07) * mm});
            skLineSegment(sketch, "E341", {"start": v(-94.54, 58.07) * mm, "end": v(-79.3, 58.07) * mm});
            skLineSegment(sketch, "E342", {"start": v(-94.54, 55.07) * mm, "end": v(-79.3, 55.07) * mm});
            skLineSegment(sketch, "E343", {"start": v(-79.3, 55.07) * mm, "end": v(-79.3, 47.45) * mm});
            skLineSegment(sketch, "E344", {"start": v(-79.3, 58.07) * mm, "end": v(-79.3, 65.69) * mm});
            skLineSegment(sketch, "E345", {"start": v(-79.3, 65.69) * mm, "end": v(-109.78, 65.69) * mm});
            skLineSegment(sketch, "E346", {"start": v(-109.78, 65.69) * mm, "end": v(-135.18, 174.45) * mm});
            skPoint(sketch, "E347.0", {"position": v(-89.96, 175.32) * mm});
            skPoint(sketch, "E348.0", {"position": v(-89.96, 172.32) * mm});
            skSolve(sketch);
        }
        {
            var Q0;
            Q0=makeQuery(id+"F14.imprint","IMPRINT",FACE,{"disambiguationData":[TD([[makeQuery(id+"F14.imprint","IMPRINT",EDGE,{"derivedFrom":sQuery(id+"F14.wireOp",EDGE,"E333")}),1.0]])]});
            extrude(context, id + "F15", {"entities" : qUnion([Q0]), "depth" : 3 * mm, "offsetDistance" : 25.4 * mm});
        }
        {
            var Q0;
            Q0=makeQuery(id+"F11.opExtrude","SWEPT_FACE",FACE,{"disambiguationData":[OSD([sQuery(id+"F10.wireOp",EDGE,"E212")])]});
            var sketch = newSketch(context, id + "F16", { "sketchPlane" : qUnion([Q0])});
            skLineSegment(sketch, "E349", {"start": v(-22.56, 52.07) * mm, "end": v(-22.56, 60.15) * mm});
            skLineSegment(sketch, "E350", {"start": v(-12.9, 55.07) * mm, "end": v(-12.9, 52.07) * mm});
            skLineSegment(sketch, "E351", {"start": v(-3.25, 52.07) * mm, "end": v(-3.25, 55.07) * mm});
            skLineSegment(sketch, "E352", {"start": v(6.4, 55.07) * mm, "end": v(6.4, 52.07) * mm});
            skLineSegment(sketch, "E353", {"start": v(16.05, 52.07) * mm, "end": v(16.05, 55.07) * mm});
            skLineSegment(sketch, "E354", {"start": v(25.7, 55.07) * mm, "end": v(25.7, 52.07) * mm});
            skLineSegment(sketch, "E355", {"start": v(-22.56, 52.07) * mm, "end": v(-12.9, 52.07) * mm});
            skLineSegment(sketch, "E356", {"start": v(-3.25, 52.07) * mm, "end": v(6.4, 52.07) * mm});
            skLineSegment(sketch, "E357", {"start": v(16.05, 52.07) * mm, "end": v(25.7, 52.07) * mm});
            skLineSegment(sketch, "E358", {"start": v(25.7, 55.07) * mm, "end": v(25.7, 60.15) * mm});
            skLineSegment(sketch, "E359", {"start": v(25.7, 60.15) * mm, "end": v(-22.56, 60.15) * mm});
            skLineSegment(sketch, "E360", {"start": v(-12.9, 55.07) * mm, "end": v(-3.25, 55.07) * mm});
            skLineSegment(sketch, "E361", {"start": v(6.4, 55.07) * mm, "end": v(16.05, 55.07) * mm});
            skPoint(sketch, "E362.0", {"position": v(-22.56, 52.07) * mm});
            skSolve(sketch);
        }
        {
            var Q0;
            Q0=makeQuery(id+"F16.imprint","IMPRINT",FACE,{"disambiguationData":[TD([[makeQuery(id+"F16.imprint","IMPRINT",EDGE,{"derivedFrom":sQuery(id+"F16.wireOp",EDGE,"E349")}),-1.0]])]});
            extrude(context, id + "F17", {"entities" : qUnion([Q0]), "depth" : 3 * mm, "offsetDistance" : 25.4 * mm});
        }
        {
            var Q0;
            Q0=makeQuery(id+"F11.opExtrude","SWEPT_FACE",FACE,{"disambiguationData":[OSD([sQuery(id+"F10.wireOp",EDGE,"E230")])]});
            var sketch = newSketch(context, id + "F18", { "sketchPlane" : qUnion([Q0])});
            skLineSegment(sketch, "E363", {"start": v(-25.7, 52.07) * mm, "end": v(-25.7, 60.15) * mm});
            skLineSegment(sketch, "E364", {"start": v(-16.05, 55.07) * mm, "end": v(-16.05, 52.07) * mm});
            skLineSegment(sketch, "E365", {"start": v(-6.4, 52.07) * mm, "end": v(-6.4, 55.07) * mm});
            skLineSegment(sketch, "E366", {"start": v(3.25, 55.07) * mm, "end": v(3.25, 52.07) * mm});
            skLineSegment(sketch, "E367", {"start": v(12.9, 52.07) * mm, "end": v(12.9, 55.07) * mm});
            skLineSegment(sketch, "E368", {"start": v(22.56, 55.07) * mm, "end": v(22.56, 52.07) * mm});
            skLineSegment(sketch, "E369", {"start": v(-25.7, 52.07) * mm, "end": v(-16.05, 52.07) * mm});
            skLineSegment(sketch, "E370", {"start": v(-6.4, 52.07) * mm, "end": v(3.25, 52.07) * mm});
            skLineSegment(sketch, "E371", {"start": v(12.9, 52.07) * mm, "end": v(22.56, 52.07) * mm});
            skLineSegment(sketch, "E372", {"start": v(22.56, 55.07) * mm, "end": v(22.56, 60.15) * mm});
            skLineSegment(sketch, "E373", {"start": v(22.56, 60.15) * mm, "end": v(-25.7, 60.15) * mm});
            skLineSegment(sketch, "E374", {"start": v(-16.05, 55.07) * mm, "end": v(-6.4, 55.07) * mm});
            skLineSegment(sketch, "E375", {"start": v(3.25, 55.07) * mm, "end": v(12.9, 55.07) * mm});
            skPoint(sketch, "E376.0", {"position": v(-25.7, 52.07) * mm});
            skSolve(sketch);
        }
        {
            var Q0;
            Q0=makeQuery(id+"F18.imprint","IMPRINT",FACE,{"disambiguationData":[TD([[makeQuery(id+"F18.imprint","IMPRINT",EDGE,{"derivedFrom":sQuery(id+"F18.wireOp",EDGE,"E363")}),-1.0]])]});
            extrude(context, id + "F19", {"entities" : qUnion([Q0]), "depth" : 3 * mm, "offsetDistance" : 25.4 * mm});
        }
        {
            var Q0;
            Q0=makeQuery(id+"F11.opExtrude","SWEPT_FACE",FACE,{"disambiguationData":[OSD([sQuery(id+"F10.wireOp",EDGE,"E248")])]});
            var sketch = newSketch(context, id + "F20", { "sketchPlane" : qUnion([Q0])});
            skLineSegment(sketch, "E377", {"start": v(-23.83, 52.07) * mm, "end": v(-23.83, 67.77) * mm});
            skLineSegment(sketch, "E378", {"start": v(-14.17, 55.07) * mm, "end": v(-14.17, 52.07) * mm});
            skLineSegment(sketch, "E379", {"start": v(-4.52, 52.07) * mm, "end": v(-4.52, 55.07) * mm});
            skLineSegment(sketch, "E380", {"start": v(5.13, 55.07) * mm, "end": v(5.13, 52.07) * mm});
            skLineSegment(sketch, "E381", {"start": v(14.78, 52.07) * mm, "end": v(14.78, 55.07) * mm});
            skLineSegment(sketch, "E382", {"start": v(24.43, 55.07) * mm, "end": v(24.43, 52.07) * mm});
            skLineSegment(sketch, "E383", {"start": v(-23.83, 52.07) * mm, "end": v(-14.17, 52.07) * mm});
            skLineSegment(sketch, "E384", {"start": v(-4.52, 52.07) * mm, "end": v(5.13, 52.07) * mm});
            skLineSegment(sketch, "E385", {"start": v(14.78, 52.07) * mm, "end": v(24.43, 52.07) * mm});
            skLineSegment(sketch, "E386", {"start": v(-14.17, 55.07) * mm, "end": v(-4.52, 55.07) * mm});
            skLineSegment(sketch, "E387", {"start": v(5.13, 55.07) * mm, "end": v(14.78, 55.07) * mm});
            skLineSegment(sketch, "E388", {"start": v(24.43, 55.07) * mm, "end": v(24.43, 67.77) * mm});
            skLineSegment(sketch, "E389", {"start": v(-1.52, 67.77) * mm, "end": v(-1.52, 57.6) * mm});
            skLineSegment(sketch, "E390", {"start": v(-1.52, 57.6) * mm, "end": v(-4.52, 57.6) * mm});
            skLineSegment(sketch, "E391", {"start": v(-4.52, 57.6) * mm, "end": v(-4.52, 67.77) * mm});
            skLineSegment(sketch, "E392", {"start": v(-4.52, 67.77) * mm, "end": v(-23.83, 67.77) * mm});
            skLineSegment(sketch, "E393", {"start": v(-1.52, 67.77) * mm, "end": v(24.43, 67.77) * mm});
            skPoint(sketch, "E394.0", {"position": v(-23.83, 52.07) * mm});
            skSolve(sketch);
        }
        {
            var Q0;
            Q0=makeQuery(id+"F20.imprint","IMPRINT",FACE,{"disambiguationData":[TD([[makeQuery(id+"F20.imprint","IMPRINT",EDGE,{"derivedFrom":sQuery(id+"F20.wireOp",EDGE,"E377")}),-1.0]])]});
            extrude(context, id + "F21", {"entities" : qUnion([Q0]), "depth" : 3 * mm, "offsetDistance" : 25.4 * mm});
        }
        {
            var Q0;
            Q0=makeQuery(id+"F11.opExtrude","SWEPT_FACE",FACE,{"disambiguationData":[OSD([sQuery(id+"F10.wireOp",EDGE,"E236")])]});
            var sketch = newSketch(context, id + "F22", { "sketchPlane" : qUnion([Q0])});
            skLineSegment(sketch, "E395", {"start": v(-23.83, 52.07) * mm, "end": v(-23.83, 67.77) * mm});
            skLineSegment(sketch, "E396", {"start": v(-14.17, 55.07) * mm, "end": v(-14.17, 52.07) * mm});
            skLineSegment(sketch, "E397", {"start": v(-4.52, 52.07) * mm, "end": v(-4.52, 55.07) * mm});
            skLineSegment(sketch, "E398", {"start": v(5.13, 55.07) * mm, "end": v(5.13, 52.07) * mm});
            skLineSegment(sketch, "E399", {"start": v(14.78, 52.07) * mm, "end": v(14.78, 55.07) * mm});
            skLineSegment(sketch, "E400", {"start": v(24.43, 55.07) * mm, "end": v(24.43, 52.07) * mm});
            skLineSegment(sketch, "E401", {"start": v(-23.83, 52.07) * mm, "end": v(-14.17, 52.07) * mm});
            skLineSegment(sketch, "E402", {"start": v(-4.52, 52.07) * mm, "end": v(5.13, 52.07) * mm});
            skLineSegment(sketch, "E403", {"start": v(14.78, 52.07) * mm, "end": v(24.43, 52.07) * mm});
            skLineSegment(sketch, "E404", {"start": v(-14.17, 55.07) * mm, "end": v(-4.52, 55.07) * mm});
            skLineSegment(sketch, "E405", {"start": v(5.13, 55.07) * mm, "end": v(14.78, 55.07) * mm});
            skLineSegment(sketch, "E406", {"start": v(24.43, 55.07) * mm, "end": v(24.43, 67.77) * mm});
            skLineSegment(sketch, "E407", {"start": v(-1.52, 67.77) * mm, "end": v(-1.52, 57.6) * mm});
            skLineSegment(sketch, "E408", {"start": v(-1.52, 57.6) * mm, "end": v(-4.52, 57.6) * mm});
            skLineSegment(sketch, "E409", {"start": v(-4.52, 57.6) * mm, "end": v(-4.52, 67.77) * mm});
            skLineSegment(sketch, "E410", {"start": v(-4.52, 67.77) * mm, "end": v(-23.83, 67.77) * mm});
            skLineSegment(sketch, "E411", {"start": v(-1.52, 67.77) * mm, "end": v(24.43, 67.77) * mm});
            skPoint(sketch, "E412.0", {"position": v(-23.83, 52.07) * mm});
            skSolve(sketch);
        }
        {
            var Q0;
            Q0=makeQuery(id+"F22.imprint","IMPRINT",FACE,{"disambiguationData":[TD([[makeQuery(id+"F22.imprint","IMPRINT",EDGE,{"derivedFrom":sQuery(id+"F22.wireOp",EDGE,"E395")}),-1.0]])]});
            extrude(context, id + "F23", {"entities" : qUnion([Q0]), "depth" : 3 * mm, "offsetDistance" : 25.4 * mm});
        }
        {
            var Q0;
            Q0=makeQuery(id+"F11.opExtrude","SWEPT_FACE",FACE,{"disambiguationData":[OSD([sQuery(id+"F10.wireOp",EDGE,"E163")])]});
            var sketch = newSketch(context, id + "F24", { "sketchPlane" : qUnion([Q0])});
            skLineSegment(sketch, "E413", {"start": v(8.72, 52.07) * mm, "end": v(3.95, 52.07) * mm});
            skLineSegment(sketch, "E414", {"start": v(3.95, 52.07) * mm, "end": v(3.95, 55.07) * mm});
            skLineSegment(sketch, "E415", {"start": v(-0.81, 55.07) * mm, "end": v(-0.81, 52.07) * mm});
            skLineSegment(sketch, "E416", {"start": v(-0.81, 52.07) * mm, "end": v(-5.58, 52.07) * mm});
            skLineSegment(sketch, "E417", {"start": v(-5.58, 52.07) * mm, "end": v(-5.58, 55.07) * mm});
            skLineSegment(sketch, "E418", {"start": v(-10.34, 55.07) * mm, "end": v(-10.34, 52.07) * mm});
            skLineSegment(sketch, "E419", {"start": v(8.72, 52.07) * mm, "end": v(8.72, 55.07) * mm});
            skLineSegment(sketch, "E420", {"start": v(13.48, 55.07) * mm, "end": v(13.48, 52.07) * mm});
            skLineSegment(sketch, "E421", {"start": v(-10.34, 52.07) * mm, "end": v(-15.1, 52.07) * mm});
            skLineSegment(sketch, "E422", {"start": v(-15.1, 52.07) * mm, "end": v(-15.1, 83.97) * mm});
            skLineSegment(sketch, "E423", {"start": v(13.48, 52.07) * mm, "end": v(18.25, 52.07) * mm});
            skLineSegment(sketch, "E424", {"start": v(18.25, 52.07) * mm, "end": v(18.25, 83.97) * mm});
            skLineSegment(sketch, "E425", {"start": v(-10.34, 55.07) * mm, "end": v(-5.58, 55.07) * mm});
            skLineSegment(sketch, "E426", {"start": v(-0.81, 55.07) * mm, "end": v(3.95, 55.07) * mm});
            skLineSegment(sketch, "E427", {"start": v(8.72, 55.07) * mm, "end": v(13.48, 55.07) * mm});
            skLineSegment(sketch, "E428", {"start": v(18.25, 83.97) * mm, "end": v(-15.1, 83.97) * mm});
            skLineSegment(sketch, "E429", {"start": v(-10.03, 60.15) * mm, "end": v(13.17, 60.15) * mm});
            skLineSegment(sketch, "E430", {"start": v(-10.03, 60.15) * mm, "end": v(-10.03, 73.83) * mm});
            skLineSegment(sketch, "E431", {"start": v(-10.03, 73.83) * mm, "end": v(13.17, 73.83) * mm});
            skLineSegment(sketch, "E432", {"start": v(13.17, 73.83) * mm, "end": v(13.17, 60.15) * mm});
            skPoint(sketch, "E433.0", {"position": v(-15.1, 52.07) * mm});
            skSolve(sketch);
        }
        {
            var Q0;
            Q0=makeQuery(id+"F24.imprint","IMPRINT",FACE,{"disambiguationData":[TD([[makeQuery(id+"F24.imprint","IMPRINT",EDGE,{"derivedFrom":sQuery(id+"F24.wireOp",EDGE,"E413")}),-1.0]])]});
            extrude(context, id + "F25", {"entities" : qUnion([Q0]), "depth" : 3 * mm, "offsetDistance" : 25.4 * mm});
        }
        {
            var Q0;
            Q0=makeQuery(id+"F11.opExtrude","SWEPT_FACE",FACE,{"disambiguationData":[OSD([sQuery(id+"F10.wireOp",EDGE,"E167")])]});
            var sketch = newSketch(context, id + "F26", { "sketchPlane" : qUnion([Q0])});
            skLineSegment(sketch, "E434", {"start": v(-83.23, 55.07) * mm, "end": v(-83.23, 52.07) * mm});
            skLineSegment(sketch, "E435", {"start": v(-83.23, 52.07) * mm, "end": v(-86.26, 52.07) * mm});
            skLineSegment(sketch, "E436", {"start": v(-86.26, 52.07) * mm, "end": v(-86.26, 55.07) * mm});
            skLineSegment(sketch, "E437", {"start": v(-89.26, 55.07) * mm, "end": v(-89.26, 52.07) * mm});
            skLineSegment(sketch, "E438", {"start": v(-89.26, 52.07) * mm, "end": v(-92.25, 52.07) * mm});
            skLineSegment(sketch, "E439", {"start": v(-92.25, 52.07) * mm, "end": v(-92.25, 55.07) * mm});
            skLineSegment(sketch, "E440", {"start": v(-95.25, 55.07) * mm, "end": v(-95.25, 52.07) * mm});
            skLineSegment(sketch, "E441", {"start": v(-95.25, 52.07) * mm, "end": v(-98.25, 52.07) * mm});
            skLineSegment(sketch, "E442", {"start": v(-98.25, 52.07) * mm, "end": v(-98.25, 79.1) * mm});
            skLineSegment(sketch, "E443", {"start": v(-77.23, 82.2) * mm, "end": v(-77.23, 52.07) * mm});
            skLineSegment(sketch, "E444", {"start": v(-77.23, 52.07) * mm, "end": v(-80.23, 52.07) * mm});
            skLineSegment(sketch, "E445", {"start": v(-80.23, 52.07) * mm, "end": v(-80.23, 55.07) * mm});
            skLineSegment(sketch, "E446", {"start": v(-95.25, 55.07) * mm, "end": v(-92.25, 55.07) * mm});
            skLineSegment(sketch, "E447", {"start": v(-89.26, 55.07) * mm, "end": v(-86.26, 55.07) * mm});
            skLineSegment(sketch, "E448", {"start": v(-83.23, 55.07) * mm, "end": v(-80.23, 55.07) * mm});
            skLineSegment(sketch, "E449", {"start": v(-82.31, 77.93) * mm, "end": v(-83.09, 75.03) * mm});
            skLineSegment(sketch, "E450", {"start": v(-82.31, 77.93) * mm, "end": v(-98.25, 82.2) * mm});
            skLineSegment(sketch, "E451", {"start": v(-83.09, 75.03) * mm, "end": v(-98.25, 79.1) * mm});
            skLineSegment(sketch, "E452", {"start": v(-98.25, 82.2) * mm, "end": v(-77.23, 82.2) * mm});
            skPoint(sketch, "E453.0", {"position": v(-98.25, 52.07) * mm});
            skSolve(sketch);
        }
        {
            var Q0;
            Q0=makeQuery(id+"F26.imprint","IMPRINT",FACE,{"disambiguationData":[TD([[makeQuery(id+"F26.imprint","IMPRINT",EDGE,{"derivedFrom":sQuery(id+"F26.wireOp",EDGE,"E434")}),-1.0]])]});
            extrude(context, id + "F27", {"entities" : qUnion([Q0]), "depth" : 3 * mm, "offsetDistance" : 25.4 * mm});
        }
        {
            var Q0;
            Q0=makeQuery(id+"F11.opExtrude","SWEPT_FACE",FACE,{"disambiguationData":[OSD([sQuery(id+"F10.wireOp",EDGE,"E265")])]});
            var sketch = newSketch(context, id + "F28", { "sketchPlane" : qUnion([Q0])});
            skLineSegment(sketch, "E454", {"start": v(-83.23, 55.07) * mm, "end": v(-83.23, 52.07) * mm});
            skLineSegment(sketch, "E455", {"start": v(-83.23, 52.07) * mm, "end": v(-86.26, 52.07) * mm});
            skLineSegment(sketch, "E456", {"start": v(-86.26, 52.07) * mm, "end": v(-86.26, 55.07) * mm});
            skLineSegment(sketch, "E457", {"start": v(-89.26, 55.07) * mm, "end": v(-89.26, 52.07) * mm});
            skLineSegment(sketch, "E458", {"start": v(-89.26, 52.07) * mm, "end": v(-92.25, 52.07) * mm});
            skLineSegment(sketch, "E459", {"start": v(-92.25, 52.07) * mm, "end": v(-92.25, 55.07) * mm});
            skLineSegment(sketch, "E460", {"start": v(-95.25, 55.07) * mm, "end": v(-95.25, 52.07) * mm});
            skLineSegment(sketch, "E461", {"start": v(-95.25, 52.07) * mm, "end": v(-98.25, 52.07) * mm});
            skLineSegment(sketch, "E462", {"start": v(-98.25, 52.07) * mm, "end": v(-98.25, 79.1) * mm});
            skLineSegment(sketch, "E463", {"start": v(-77.23, 82.2) * mm, "end": v(-77.23, 52.07) * mm});
            skLineSegment(sketch, "E464", {"start": v(-77.23, 52.07) * mm, "end": v(-80.23, 52.07) * mm});
            skLineSegment(sketch, "E465", {"start": v(-80.23, 52.07) * mm, "end": v(-80.23, 55.07) * mm});
            skLineSegment(sketch, "E466", {"start": v(-95.25, 55.07) * mm, "end": v(-92.25, 55.07) * mm});
            skLineSegment(sketch, "E467", {"start": v(-89.26, 55.07) * mm, "end": v(-86.26, 55.07) * mm});
            skLineSegment(sketch, "E468", {"start": v(-83.23, 55.07) * mm, "end": v(-80.23, 55.07) * mm});
            skLineSegment(sketch, "E469", {"start": v(-82.31, 77.93) * mm, "end": v(-83.09, 75.03) * mm});
            skLineSegment(sketch, "E470", {"start": v(-82.31, 77.93) * mm, "end": v(-98.25, 82.2) * mm});
            skLineSegment(sketch, "E471", {"start": v(-83.09, 75.03) * mm, "end": v(-98.25, 79.1) * mm});
            skLineSegment(sketch, "E472", {"start": v(-98.25, 82.2) * mm, "end": v(-77.23, 82.2) * mm});
            skPoint(sketch, "E473.0", {"position": v(-98.25, 52.07) * mm});
            skSolve(sketch);
        }
        {
            var Q0;
            Q0=makeQuery(id+"F28.imprint","IMPRINT",FACE,{"disambiguationData":[TD([[makeQuery(id+"F28.imprint","IMPRINT",EDGE,{"derivedFrom":sQuery(id+"F28.wireOp",EDGE,"E454")}),-1.0]])]});
            extrude(context, id + "F29", {"entities" : qUnion([Q0]), "depth" : 3 * mm, "offsetDistance" : 25.4 * mm});
        }
        {
            var Q0;
            Q0=makeQuery(id+"F11.opExtrude","SWEPT_FACE",FACE,{"disambiguationData":[OSD([sQuery(id+"F10.wireOp",EDGE,"E137")])]});
            var sketch = newSketch(context, id + "F30", { "sketchPlane" : qUnion([Q0])});
            skLineSegment(sketch, "E474", {"start": v(13.48, 81.47) * mm, "end": v(-10.34, 81.47) * mm});
            skCircle(sketch, "E475", {"center": v(1.57, 69.56) * mm, "radius": 3.04 * mm});
            skCircle(sketch, "E476", {"center": v(9.05, 69.56) * mm, "radius": 0.5 * mm});
            skCircle(sketch, "E477", {"center": v(-5.9, 69.56) * mm, "radius": 0.5 * mm});
            skLineSegment(sketch, "E478", {"start": v(8.72, 54.61) * mm, "end": v(8.72, 57.6) * mm});
            skLineSegment(sketch, "E479", {"start": v(8.72, 57.6) * mm, "end": v(3.95, 57.6) * mm});
            skLineSegment(sketch, "E480", {"start": v(3.95, 57.6) * mm, "end": v(3.95, 54.61) * mm});
            skLineSegment(sketch, "E481", {"start": v(-0.81, 54.61) * mm, "end": v(-0.81, 57.6) * mm});
            skLineSegment(sketch, "E482", {"start": v(-0.81, 57.6) * mm, "end": v(-5.58, 57.6) * mm});
            skLineSegment(sketch, "E483", {"start": v(-5.58, 57.6) * mm, "end": v(-5.58, 54.61) * mm});
            skLineSegment(sketch, "E484", {"start": v(13.48, 52.07) * mm, "end": v(-10.34, 52.07) * mm});
            skLineSegment(sketch, "E485", {"start": v(-10.34, 81.47) * mm, "end": v(-10.34, 52.07) * mm});
            skLineSegment(sketch, "E486", {"start": v(13.48, 81.47) * mm, "end": v(13.48, 52.07) * mm});
            skLineSegment(sketch, "E487", {"start": v(-5.58, 54.61) * mm, "end": v(-0.81, 54.61) * mm});
            skLineSegment(sketch, "E488", {"start": v(3.95, 54.61) * mm, "end": v(8.72, 54.61) * mm});
            skPoint(sketch, "E489.0", {"position": v(-10.34, 52.07) * mm});
            skSolve(sketch);
        }
        {
            var Q0;
            Q0=makeQuery(id+"F30.imprint","IMPRINT",FACE,{"disambiguationData":[TD([[makeQuery(id+"F30.imprint","IMPRINT",EDGE,{"derivedFrom":sQuery(id+"F30.wireOp",EDGE,"E474")}),1.0]])]});
            extrude(context, id + "F31", {"entities" : qUnion([Q0]), "depth" : 3 * mm, "offsetDistance" : 25.4 * mm});
        }
    });
